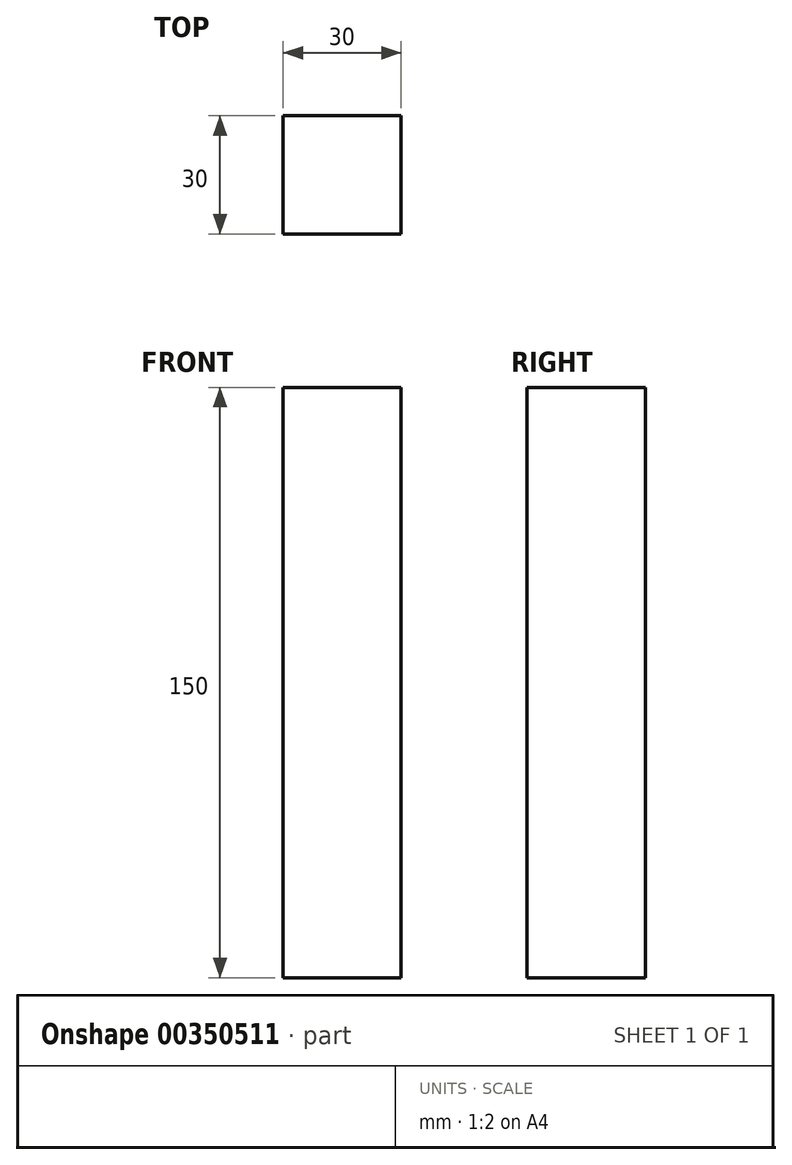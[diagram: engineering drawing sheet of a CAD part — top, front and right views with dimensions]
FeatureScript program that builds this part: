
annotation { "Feature Type Name" : "Feature", "Feature Type Description" : "" }
export const myFeature = defineFeature(function(context is Context, id is Id, definition is map)
    precondition{}
    {
        {
            var Q0;
            Q0=qCreatedBy(makeId("Top.planeOp"),FACE);
            var sketch = newSketch(context, id + "F0", { "sketchPlane" : qUnion([Q0])});
            skLineSegment(sketch, "E0.bottom", {"start": v(15, 15) * mm, "end": v(-15, 15) * mm});
            skLineSegment(sketch, "E0.top", {"start": v(15, -15) * mm, "end": v(-15, -15) * mm});
            skLineSegment(sketch, "E0.left", {"start": v(15, 15) * mm, "end": v(15, -15) * mm});
            skLineSegment(sketch, "E0.right", {"start": v(-15, 15) * mm, "end": v(-15, -15) * mm});
            skPoint(sketch, "E0.middle", {"position": v(0, 0) * mm});
            skSolve(sketch);
        }
        {
            var Q0;
            Q0=makeQuery(id+"F0.imprint","IMPRINT",FACE,{"disambiguationData":[TD([[makeQuery(id+"F0.imprint","IMPRINT",EDGE,{"derivedFrom":sQuery(id+"F0.wireOp",EDGE,"E0.bottom")}),1.0]])]});
            extrude(context, id + "F1", {"entities" : qUnion([Q0]), "endBound" : BoundingType.SYMMETRIC, "depth" : 150 * mm});
        }
    });
